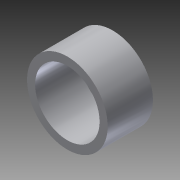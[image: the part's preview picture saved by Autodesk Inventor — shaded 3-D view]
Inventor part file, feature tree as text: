
AUTODESK INVENTOR PART (.ipt)
format: ipt  version: 2014 SP1 (Build 180222100, 222)  size: 85,504 bytes
history: native  units: in
note: dims shown in document units (in); Inventor stores cm internally (conversion verified against a paired STEP export)
features: extrude x1, sketch x1
ambient origin geometry x8: Origin, YZ Plane, XZ Plane, XY Plane, X Axis, Y Axis, Z Axis, Center Point
bodies: Solid1 (feature_tree)
feature tree (2):
  extrude  "Extrusion1"  Depth=0.3508in
  sketch  "Sketch1"  dims[d0=0.625in d1=0.5in d2=0.3508in d3=0.0in]
